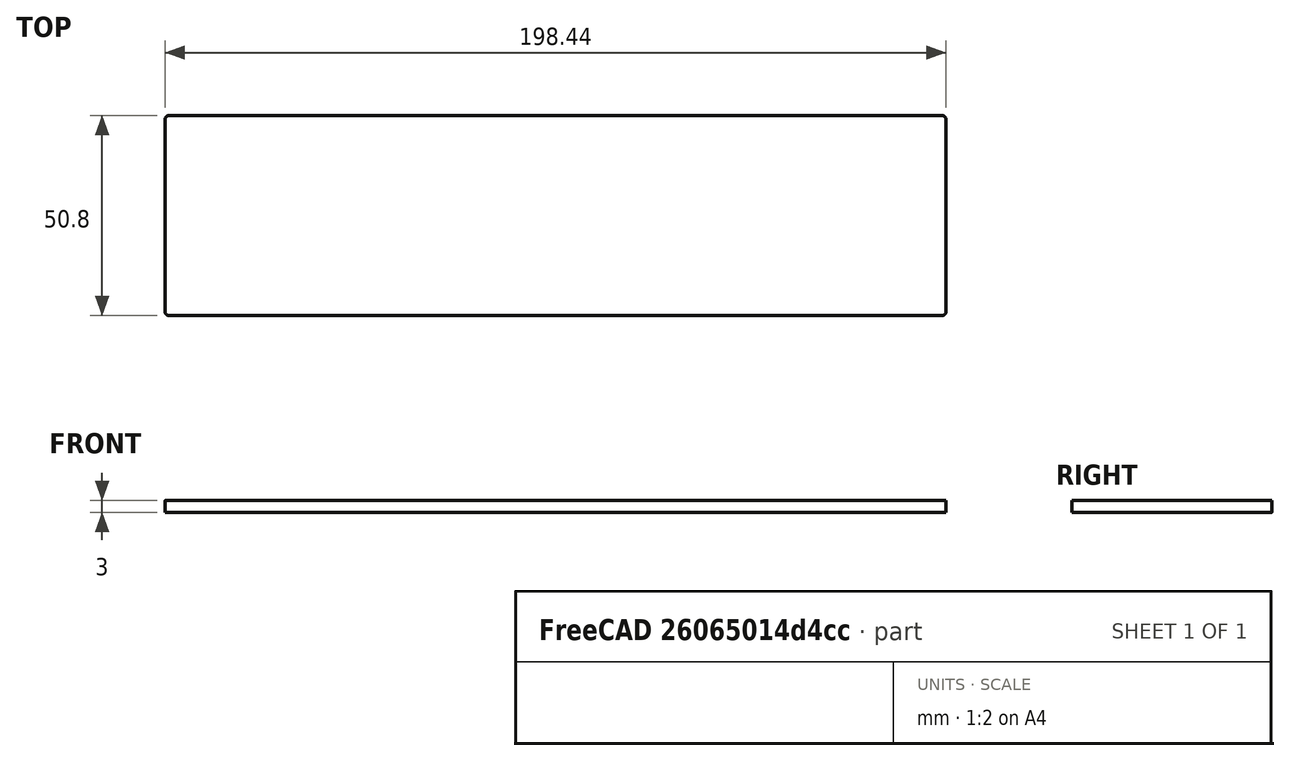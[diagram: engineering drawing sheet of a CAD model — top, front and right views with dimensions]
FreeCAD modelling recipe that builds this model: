
FCSTD DOCUMENT  (FreeCAD 0.21R33675 (Git))
Label: floor
License: All rights reserved
LicenseURL: http://en.wikipedia.org/wiki/All_rights_reserved
objects: Spreadsheet::Sheet×1, Sketcher::SketchObject×1, PartDesign::Pad×1, PartDesign::Body×1
note: 4 computed .brp shape members not serialized (recipe doc carries the construction recipe); baked Part::Feature solids carry a one-line shape summary decoded from their .brp

FEATURE [Spreadsheet::Sheet] Spreadsheet
  cells = A2='Design Parameters; A3='Length; B3(Length)==7.8125 in; A4='Width; B4(Width)==2 in; A5='Thickness; B5(Thickness)==3 mm; A6='FilletRadius; B6(FilletRadius)==1 mm
FEATURE [Sketcher::SketchObject] Sketch  label="FloorSketch"
  FullyConstrained = true
  MapMode = 5
  Support = -> [XY_Plane]
  expr: Constraints[20] = Spreadsheet.FilletRadius
  expr: Constraints[21] = Spreadsheet.Length
  expr: Constraints[22] = Spreadsheet.Width
  sketch-geometry (10):
    g0: ArcOfCircle CenterX=1 CenterY=1 CenterZ=0 NormalX=0 NormalY=0 NormalZ=1 AngleXU=0 Radius=1 StartAngle=3.14159 EndAngle=4.71239
    g1: LineSegment StartX=6.06e-14 StartY=1 StartZ=0 EndX=6.06e-14 EndY=49.8 EndZ=0
    g2: ArcOfCircle CenterX=1 CenterY=49.8 CenterZ=0 NormalX=0 NormalY=0 NormalZ=1 AngleXU=0 Radius=1 StartAngle=1.5708 EndAngle=3.14159
    g3: LineSegment StartX=1 StartY=50.8 StartZ=0 EndX=197.438 EndY=50.8 EndZ=0
    g4: ArcOfCircle CenterX=197.437 CenterY=49.8 CenterZ=0 NormalX=0 NormalY=0 NormalZ=1 AngleXU=0 Radius=1 StartAngle=-2.16e-12 EndAngle=1.5708
    g5: LineSegment StartX=198.438 StartY=49.8 StartZ=0 EndX=198.438 EndY=1 EndZ=0
    g6: ArcOfCircle CenterX=197.437 CenterY=1 CenterZ=0 NormalX=0 NormalY=0 NormalZ=1 AngleXU=0 Radius=1 StartAngle=4.71239 EndAngle=6.28319
    g7: LineSegment StartX=197.438 StartY=9.439e-13 StartZ=0 EndX=1 EndY=9.439e-13 EndZ=0
    g8: GeomPoint X=0 Y=0 Z=0
    g9: GeomPoint X=198.438 Y=50.8 Z=0
  constraints (23):
    c: Tangent(g0,g1) = 1.5708
    c: Tangent(g1,g2) = 1.5708
    c: Tangent(g2,g3) = 1.5708
    c: Tangent(g3,g4) = 1.5708
    c: Tangent(g4,g5) = 1.5708
    c: Tangent(g5,g6) = 1.5708
    c: Tangent(g6,g7) = 1.5708
    c: Tangent(g7,g0) = 1.5708
    c: Horizontal(g3)
    c: Horizontal(g7)
    c: Vertical(g1)
    c: Vertical(g5)
    c: Equal(g0,g2)
    c: Equal(g2,g4)
    c: Equal(g4,g6)
    c: PointOnObject(g8,g1)
    c: PointOnObject(g8,g7)
    c: PointOnObject(g9,g3)
    c: PointOnObject(g9,g5)
    c: Coincident(g8,g-1)
    c: Radius(g4) = 1
    c: DistanceX(g0,g5) = 198.438
    c: DistanceY(g6,g3) = 50.8
FEATURE [PartDesign::Pad] Pad  label="FloorPad"
  Direction = (0,0,1)
  Length = 3
  Length2 = 10
  Profile = -> Sketch
  ReferenceAxis = -> Sketch [N_Axis]
  Type = 0
  expr: Length = Spreadsheet.Thickness
FEATURE [PartDesign::Body] Body
  Group = -> [Sketch,Pad]
  Origin = -> Origin
  Tip = -> Pad
